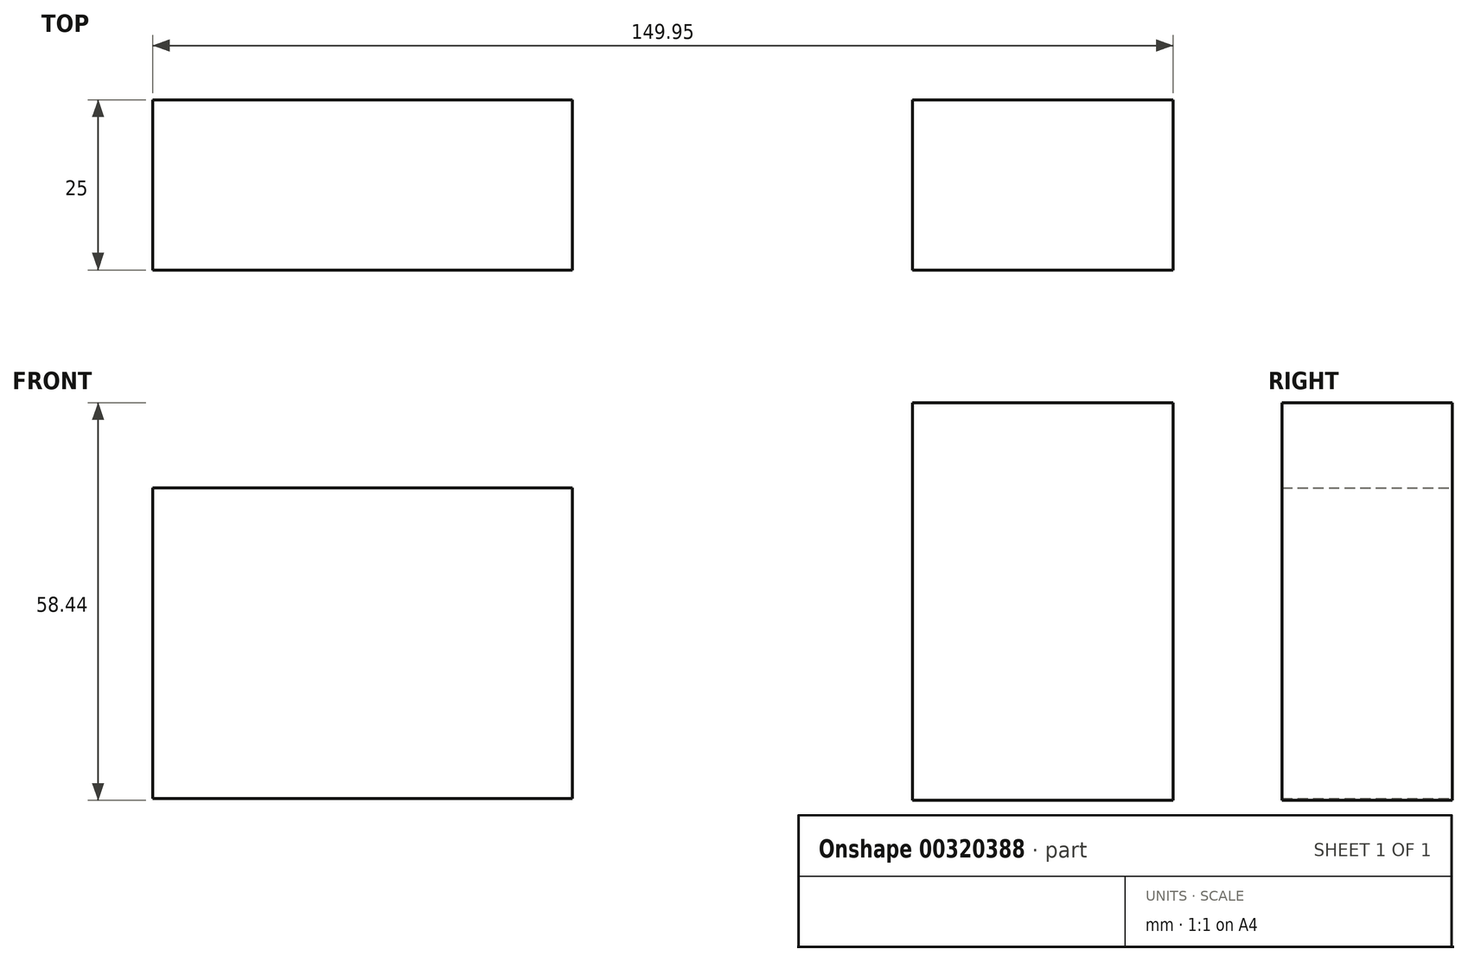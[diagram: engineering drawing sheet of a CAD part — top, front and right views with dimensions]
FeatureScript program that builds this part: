
annotation { "Feature Type Name" : "Feature", "Feature Type Description" : "" }
export const myFeature = defineFeature(function(context is Context, id is Id, definition is map)
    precondition{}
    {
        {
            var Q0;
            Q0=qCreatedBy(makeId("Front.planeOp"),FACE);
            var sketch = newSketch(context, id + "F0", { "sketchPlane" : qUnion([Q0])});
            skLineSegment(sketch, "E0.bottom", {"start": v(-96.72, -19.48) * mm, "end": v(-35.05, -19.48) * mm});
            skLineSegment(sketch, "E0.top", {"start": v(-96.72, 26.23) * mm, "end": v(-35.05, 26.23) * mm});
            skLineSegment(sketch, "E0.left", {"start": v(-96.72, -19.48) * mm, "end": v(-96.72, 26.23) * mm});
            skLineSegment(sketch, "E0.right", {"start": v(-35.05, -19.48) * mm, "end": v(-35.05, 26.23) * mm});
            skPoint(sketch, "E0.middle", {"position": v(-65.89, 3.38) * mm});
            skLineSegment(sketch, "E1.bottom", {"start": v(14.93, -19.7) * mm, "end": v(53.23, -19.7) * mm});
            skLineSegment(sketch, "E1.top", {"start": v(14.93, 38.73) * mm, "end": v(53.23, 38.73) * mm});
            skLineSegment(sketch, "E1.left", {"start": v(14.93, -19.7) * mm, "end": v(14.93, 38.73) * mm});
            skLineSegment(sketch, "E1.right", {"start": v(53.23, -19.7) * mm, "end": v(53.23, 38.73) * mm});
            skPoint(sketch, "E1.middle", {"position": v(34.08, 9.51) * mm});
            skSolve(sketch);
        }
        {
            var Q0;
            Q0=makeQuery(id+"F0.imprint","IMPRINT",FACE,{"disambiguationData":[TD([[makeQuery(id+"F0.imprint","IMPRINT",EDGE,{"derivedFrom":sQuery(id+"F0.wireOp",EDGE,"E1.bottom")}),1.0]])]});
            var Q1;
            Q1=makeQuery(id+"F0.imprint","IMPRINT",FACE,{"disambiguationData":[TD([[makeQuery(id+"F0.imprint","IMPRINT",EDGE,{"derivedFrom":sQuery(id+"F0.wireOp",EDGE,"E0.bottom")}),1.0]])]});
            extrude(context, id + "F1", {"entities" : qUnion([Q0, Q1]), "depth" : 25 * mm});
        }
    });
